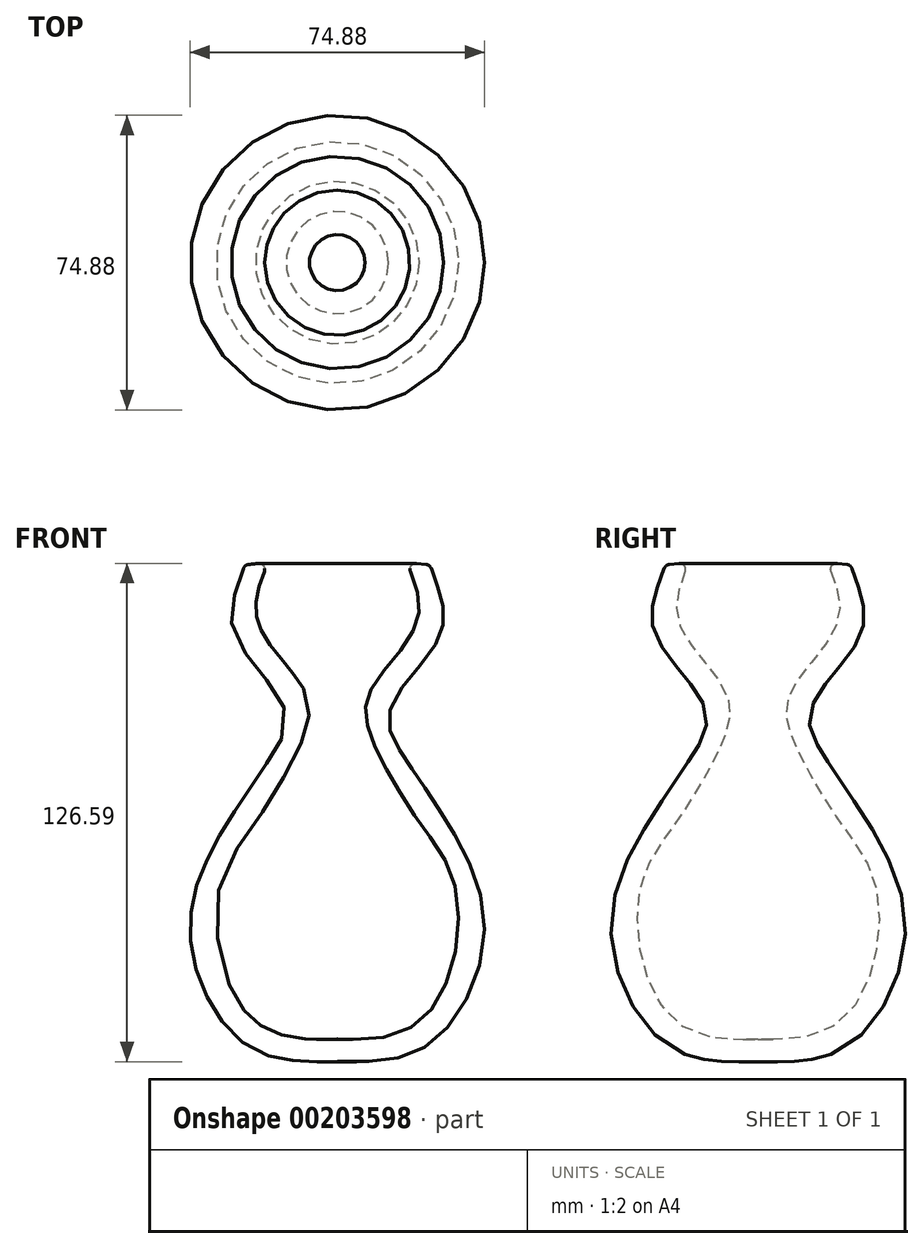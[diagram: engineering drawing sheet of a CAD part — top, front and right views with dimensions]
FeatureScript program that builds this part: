
annotation { "Feature Type Name" : "Feature", "Feature Type Description" : "" }
export const myFeature = defineFeature(function(context is Context, id is Id, definition is map)
    precondition{}
    {
        {
            var Q0;
            Q0=qCreatedBy(makeId("Front.planeOp"),FACE);
            var sketch = newSketch(context, id + "F0", { "sketchPlane" : qUnion([Q0])});
            skFitSpline(sketch, "E0", {"points": [v(0, -34.44) * mm, v(23.9, -29.73) * mm, v(37.43, 0) * mm, v(26.74, 28.15) * mm, v(17.3, 42.3) * mm, v(13.21, 54.26) * mm, v(24.54, 70.93) * mm, v(26.74, 81.63) * mm, v(23.6, 91.7) * mm], "startDerivative": vector(191.44, -4.88) * mm, "endDerivative": vector(-21.19, 81.56) * mm});
            skFitSpline(sketch, "E1", {"points": [v(17.62, 92.32) * mm, v(20.76, 81.32) * mm, v(17.62, 72.2) * mm, v(8.8, 60.55) * mm, v(7.24, 52.69) * mm, v(11.95, 40.74) * mm, v(21.08, 25.95) * mm, v(29.88, 10.22) * mm, v(27.37, -15.26) * mm, v(13.84, -27.84) * mm, v(0, -28.78) * mm, v(0, -29.41) * mm], "startDerivative": vector(52.76, -130.97) * mm, "endDerivative": vector(0, -92.84) * mm});
            skLineSegment(sketch, "E2", {"start": v(17.62, 92.32) * mm, "end": v(23.6, 91.7) * mm});
            skLineSegment(sketch, "E3", {"start": v(0, -34.44) * mm, "end": v(0, -28.78) * mm});
            skSolve(sketch);
        }
        {
            var Q0;
            {var subQ1=sQuery(id+"F0.wireOp",EDGE,"E0");Q0=makeQuery(id+"F0.imprint","IMPRINT",FACE,{"disambiguationData":[TD([[makeQuery(id+"F0.imprint","IMPRINT",EDGE,{"derivedFrom":subQ1}),1.0]])]});}
            var Q1;
            Q1=sQuery(id+"F0.wireOp",EDGE,"E3");
            revolve(context, id + "F1", {"entities" : qUnion([Q0]), "axis" : qUnion([Q1]), "revolveType" : RevolveType.FULL});
        }
        {
            var Q0;
            Q0=makeQuery(id+"F1.opRevolve","SWEPT_EDGE",EDGE,{"disambiguationData":[OSD([sQuery(id+"F0.wireOp",EDGE,"E0"),sQuery(id+"F0.wireOp",EDGE,"E2")])]});
            var Q1;
            Q1=makeQuery(id+"F1.opRevolve","SWEPT_EDGE",EDGE,{"disambiguationData":[OSD([sQuery(id+"F0.wireOp",EDGE,"E1"),sQuery(id+"F0.wireOp",EDGE,"E2")])]});
            fillet(context, id + "F2", {"entities" : qUnion([Q0, Q1]), "radius" : 1.52 * mm, "tangentPropagation" : true, "allowEdgeOverflow" : false});
        }
    });
